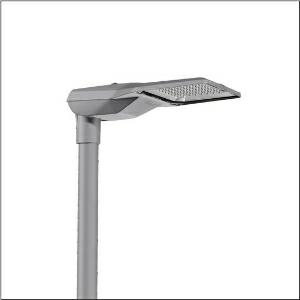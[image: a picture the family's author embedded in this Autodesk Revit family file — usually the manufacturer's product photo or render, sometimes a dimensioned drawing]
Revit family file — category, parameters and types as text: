
# Revit family: streetlight_sl_21_midi___p0_8a_5xe3u33s08lb_a919
name_source: partatom
category: Lighting Fixtures
units: mm (PartAtom-declared; Revit-internal decimal feet)

## family parameters
Cut with Voids When Loaded = No
Host = Face
Light Source = No
Part Type = Normal
Room Calculation Point = No
Round Connector Dimension = Use Diameter
Shared = No

## types (1)
- --- (1 x LED, 14470 lm, 99.6 W, 3000K)
    Apparent Load = 100 VA
    CIE Flux Codes = 33 69 96 100 100
    Color Rendering = 70
    Color Temperature = 3000K
    Default Elevation = 1800 mm
    Description = Streetlight SL 21 midi, mast luminaire, primary light control with lens, of PMMA, primary optical cover: cover, of toughened safety glass, transparent, light distribution: P0.8a, light emission: direct distribution, primary light characteristic: asymmetric, installation type: post-top, side-entry, LED, High Power LED, rated luminous flux: 14.470lm, luminous efficacy: 145lm/W, light colour: 730, colour temperature: 3000K, control gear: D4i, control: pre-setting: logarithmic dimming characteristic, flexible luminous flux parameterisation, time-dependent luminous flux control, constant luminous flux control, overheat protection, mains connection: 230..240V, AC, 50/60Hz, start of lifetime: 100W, end of service life: 102W, reduction: 46W, luminaire housing, of diecast aluminium, powder-coated, Siteco® metallic grey (DB 702S), corrosivity category C5 mid according to DIN EN ISO 12944, multi-level sealing system, sealing non-destructively replaceable, inclination adjustable: 0°, 5°, 10°, 15°, please order mast flange separately, length: 644mm, width: 335mm, height: 110mm, mast flange for spigot size: 42mm (side-entry): 5XC10008XM4, 60/48mm (side-entry/post-top): 5XC10108XM2, 76/60mm (side-entry/post-top): 5XC10108XM1, mounting height: 4..8m, Smart Interface above, protection rating (complete): IP66, insulation class (complete): insulation class II (safety insulation), certification: CE, ENEC, ENEC+, VDE, impact resistance: IK10, permissible operating ambient temperature for outdoor applications: -40..+50°C, standard-compliant lighting for roads and squares, packaging unit: 1 piece

Light Distribution: P0.8a
    Height = 111 mm
    Lamp = 1 x LED
    Lamp Light Flux = 14470 lm
    Lamp Power = 99.6 W
    Lamp count = 1
    Length = 644 mm
    Luminous efficacy = 145 lm/W
    Manufacturer = Siteco
    ModVariant = No
    Model = 5XE3U33S08LB
    Number of Poles = 1
    OnlyDefault = Yes
    Power Factor = 1
    Product Name = Streetlight SL 21 midi | P0.8a
    Product group = mast luminaire | pylon top
    ProductGroupID = 6100
    Protection Class = Protection class II
    Protection Degree = IP 66
    RLX_Detail_Level = 1
    RLX_Emergency_Light_Flux = 0 lm
    RLX_Emergency_Type = 0
    RLX_Emergency_Type_DB = No
    RlxData = <blob elided: 26609 chars, md5=b3e697d1>
    Socket = socket
    Standby Power = 0 W
    System Light Flux = 14470 lm
    System Power = 100 W
    Type Comments = factory setting: luminous flux: 100 % | dim-lin: 254 | 1020 mA
    Type Image = l_1004302.jpg
    URL = http://relux.com
    VarID = @adj_033433
    Voltage = 0 V
    Weight = 0.00 kg
    Width = 336 mm

## geometry (parser evidence)
native form markers: Blend x4, Sweep x12
no freeform markers — native parametric forms only
